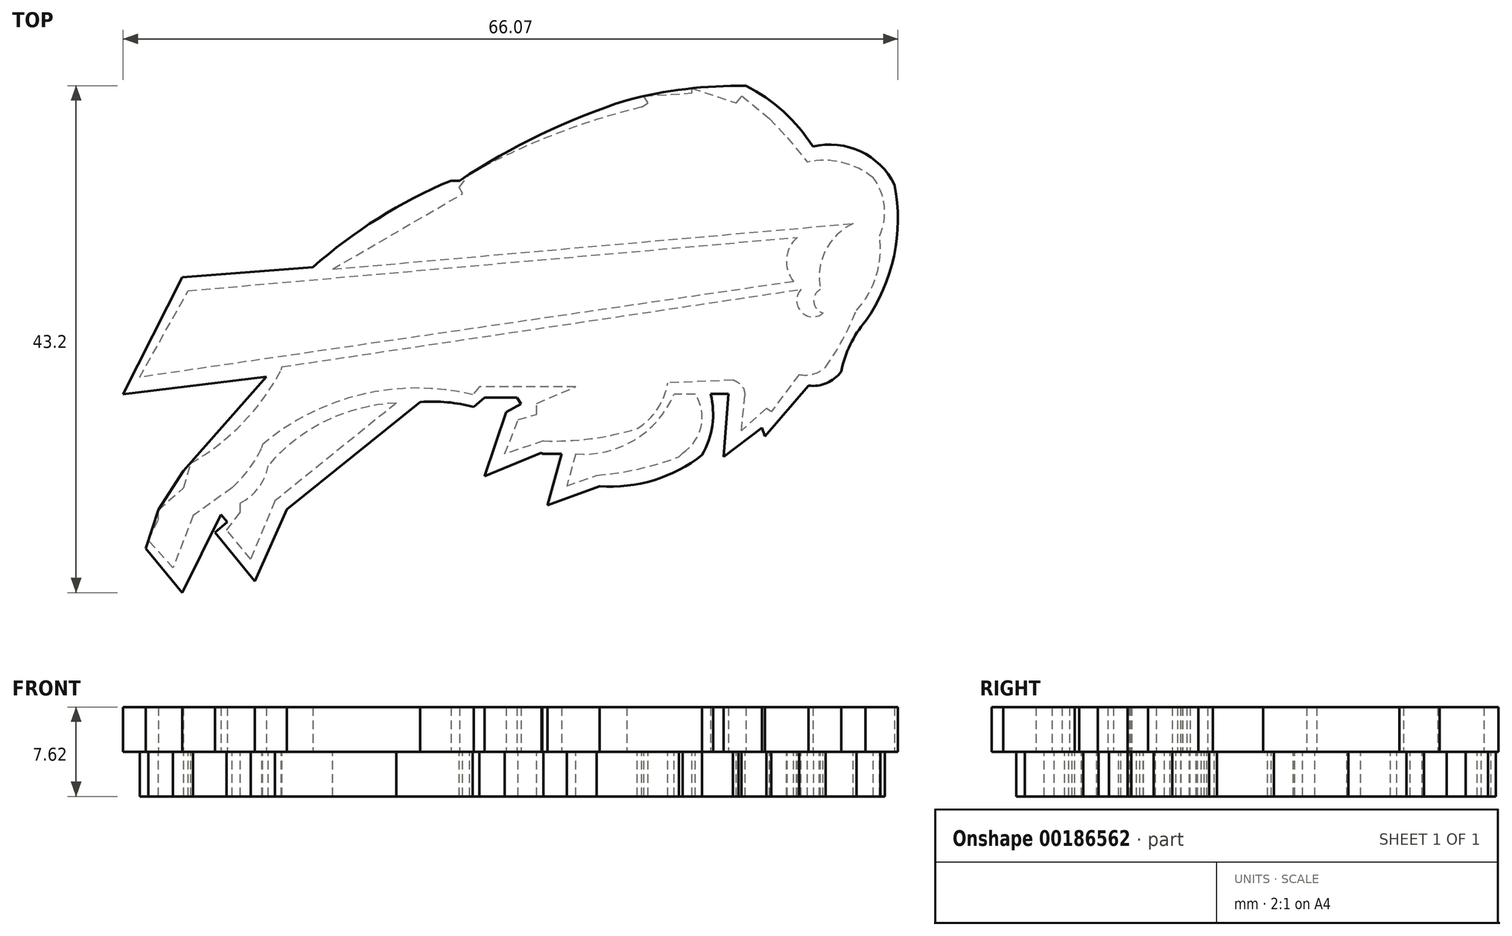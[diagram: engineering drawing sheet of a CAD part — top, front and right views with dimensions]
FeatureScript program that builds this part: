
annotation { "Feature Type Name" : "Feature", "Feature Type Description" : "" }
export const myFeature = defineFeature(function(context is Context, id is Id, definition is map)
    precondition{}
    {
        {
            var Q0;
            Q0=qCreatedBy(makeId("Top.planeOp"),FACE);
            var sketch = newSketch(context, id + "F0", { "sketchPlane" : qUnion([Q0])});
            skLineSegment(sketch, "E0", {"start": v(19.7, -52.96) * mm, "end": v(31.08, -43.8) * mm});
            skArc(sketch, "E1", {"start": v(35.62, -44.21) * mm, "mid": v(33.37, -43.82) * mm, "end": v(31.08, -43.8) * mm});
            skLineSegment(sketch, "E2", {"start": v(35.62, -44.21) * mm, "end": v(36.54, -43.41) * mm});
            skLineSegment(sketch, "E3", {"start": v(36.54, -43.41) * mm, "end": v(39.3, -43.41) * mm});
            skLineSegment(sketch, "E4", {"start": v(39.3, -43.41) * mm, "end": v(39.66, -43.95) * mm});
            skLineSegment(sketch, "E5", {"start": v(39.66, -43.95) * mm, "end": v(38.4, -44.66) * mm});
            skLineSegment(sketch, "E6", {"start": v(38.4, -44.66) * mm, "end": v(36.54, -50.13) * mm});
            skLineSegment(sketch, "E7", {"start": v(36.54, -50.13) * mm, "end": v(41.41, -48.1) * mm});
            skLineSegment(sketch, "E8", {"start": v(41.41, -48.1) * mm, "end": v(41.46, -48.23) * mm});
            skLineSegment(sketch, "E9", {"start": v(41.46, -48.23) * mm, "end": v(43.12, -48.23) * mm});
            skLineSegment(sketch, "E10", {"start": v(43.12, -48.23) * mm, "end": v(41.9, -52.58) * mm});
            skLineSegment(sketch, "E11", {"start": v(41.9, -52.58) * mm, "end": v(46.38, -50.97) * mm});
            skArc(sketch, "E12", {"start": v(46.38, -50.97) * mm, "mid": v(51, -50.46) * mm, "end": v(55.1, -48.3) * mm});
            skArc(sketch, "E13", {"start": v(55.1, -48.3) * mm, "mid": v(55.97, -45.78) * mm, "end": v(55.83, -43.1) * mm});
            skLineSegment(sketch, "E14", {"start": v(55.83, -43.1) * mm, "end": v(57.36, -43.1) * mm});
            skLineSegment(sketch, "E15", {"start": v(56.93, -48.45) * mm, "end": v(57.36, -43.1) * mm});
            skLineSegment(sketch, "E16", {"start": v(56.93, -48.45) * mm, "end": v(60.22, -46) * mm});
            skLineSegment(sketch, "E17", {"start": v(60.22, -46) * mm, "end": v(60.46, -46.7) * mm});
            skLineSegment(sketch, "E18", {"start": v(60.46, -46.7) * mm, "end": v(64.17, -42.4) * mm});
            skArc(sketch, "E19", {"start": v(64.17, -42.4) * mm, "mid": v(65.73, -42.18) * mm, "end": v(66.96, -41.19) * mm});
            skArc(sketch, "E20", {"start": v(69.03, -36.9) * mm, "mid": v(67.73, -38.92) * mm, "end": v(66.96, -41.19) * mm});
            skArc(sketch, "E21", {"start": v(69.03, -36.9) * mm, "mid": v(71.47, -31.35) * mm, "end": v(71.51, -25.29) * mm});
            skArc(sketch, "E22", {"start": v(71.51, -25.29) * mm, "mid": v(68.6, -22.42) * mm, "end": v(64.55, -22.02) * mm});
            skArc(sketch, "E23", {"start": v(64.55, -22.02) * mm, "mid": v(62.04, -19.04) * mm, "end": v(58.83, -16.84) * mm});
            skLineSegment(sketch, "E24", {"start": v(19.7, -52.96) * mm, "end": v(16.98, -59.06) * mm});
            skLineSegment(sketch, "E25", {"start": v(16.98, -59.06) * mm, "end": v(13.55, -54.9) * mm});
            skLineSegment(sketch, "E26", {"start": v(13.55, -54.9) * mm, "end": v(14.6, -54.03) * mm});
            skLineSegment(sketch, "E27", {"start": v(14.6, -54.03) * mm, "end": v(14.08, -53.4) * mm});
            skPoint(sketch, "E27.endSnap0", {"position": v(14.08, -54.46) * mm});
            skLineSegment(sketch, "E28", {"start": v(14.08, -53.4) * mm, "end": v(10.77, -60.04) * mm});
            skLineSegment(sketch, "E29", {"start": v(10.77, -60.04) * mm, "end": v(7.65, -56.27) * mm});
            skLineSegment(sketch, "E30", {"start": v(7.65, -56.27) * mm, "end": v(8.73, -52.98) * mm});
            skLineSegment(sketch, "E31", {"start": v(8.73, -52.98) * mm, "end": v(10.87, -49.66) * mm});
            skLineSegment(sketch, "E32", {"start": v(10.87, -49.66) * mm, "end": v(17.94, -41.63) * mm});
            skLineSegment(sketch, "E33", {"start": v(17.94, -41.63) * mm, "end": v(5.73, -43.13) * mm});
            skLineSegment(sketch, "E34", {"start": v(5.73, -43.13) * mm, "end": v(10.77, -33.17) * mm});
            skLineSegment(sketch, "E35", {"start": v(10.77, -33.17) * mm, "end": v(21.9, -32.31) * mm});
            skArc(sketch, "E36", {"start": v(33.68, -24.92) * mm, "mid": v(27.49, -28.14) * mm, "end": v(21.9, -32.31) * mm});
            skArc(sketch, "E37", {"start": v(48.67, -18.07) * mm, "mid": v(41.31, -21) * mm, "end": v(34.43, -24.92) * mm});
            skArc(sketch, "E38", {"start": v(58.83, -16.84) * mm, "mid": v(53.7, -17.12) * mm, "end": v(48.67, -18.07) * mm});
            skLineSegment(sketch, "E39", {"start": v(33.68, -24.92) * mm, "end": v(34.43, -24.92) * mm});
            skSolve(sketch);
        }
        {
            var Q0;
            Q0 = qSketchRegion(id + "F0", true);
            extrude(context, id + "F1", {"entities" : qUnion([Q0]), "depth" : 3.8 * mm});
        }
        {
            var Q0;
            Q0=makeQuery(id+"F1.opExtrude","CAP_FACE",FACE,{"disambiguationData":[OSD([sQuery(id+"F0.wireOp",EDGE,"E0"),sQuery(id+"F0.wireOp",EDGE,"E1"),sQuery(id+"F0.wireOp",EDGE,"E2"),sQuery(id+"F0.wireOp",EDGE,"E3"),sQuery(id+"F0.wireOp",EDGE,"E4"),sQuery(id+"F0.wireOp",EDGE,"E5"),sQuery(id+"F0.wireOp",EDGE,"E6"),sQuery(id+"F0.wireOp",EDGE,"E7"),sQuery(id+"F0.wireOp",EDGE,"E8"),sQuery(id+"F0.wireOp",EDGE,"E9"),sQuery(id+"F0.wireOp",EDGE,"E10"),sQuery(id+"F0.wireOp",EDGE,"E11"),sQuery(id+"F0.wireOp",EDGE,"E12"),sQuery(id+"F0.wireOp",EDGE,"E13"),sQuery(id+"F0.wireOp",EDGE,"E14"),sQuery(id+"F0.wireOp",EDGE,"E15"),sQuery(id+"F0.wireOp",EDGE,"E16"),sQuery(id+"F0.wireOp",EDGE,"E17"),sQuery(id+"F0.wireOp",EDGE,"E18"),sQuery(id+"F0.wireOp",EDGE,"E19"),sQuery(id+"F0.wireOp",EDGE,"E20"),sQuery(id+"F0.wireOp",EDGE,"E21"),sQuery(id+"F0.wireOp",EDGE,"E22"),sQuery(id+"F0.wireOp",EDGE,"E23"),sQuery(id+"F0.wireOp",EDGE,"E24"),sQuery(id+"F0.wireOp",EDGE,"E25"),sQuery(id+"F0.wireOp",EDGE,"E26"),sQuery(id+"F0.wireOp",EDGE,"E27"),sQuery(id+"F0.wireOp",EDGE,"E28"),sQuery(id+"F0.wireOp",EDGE,"E29"),sQuery(id+"F0.wireOp",EDGE,"E30"),sQuery(id+"F0.wireOp",EDGE,"E31"),sQuery(id+"F0.wireOp",EDGE,"E32"),sQuery(id+"F0.wireOp",EDGE,"E33"),sQuery(id+"F0.wireOp",EDGE,"E34"),sQuery(id+"F0.wireOp",EDGE,"E35"),sQuery(id+"F0.wireOp",EDGE,"E36"),sQuery(id+"F0.wireOp",EDGE,"E37"),sQuery(id+"F0.wireOp",EDGE,"E38"),sQuery(id+"F0.wireOp",EDGE,"E39")])],"isStart":true});
            var sketch = newSketch(context, id + "F2", { "sketchPlane" : qUnion([Q0])});
            skArc(sketch, "E40", {"start": v(64.07, 23.34) * mm, "mid": v(67.04, 23.38) * mm, "end": v(69.7, 24.68) * mm});
            skArc(sketch, "E41", {"start": v(69.7, 24.68) * mm, "mid": v(70.64, 27.08) * mm, "end": v(70.23, 29.63) * mm});
            skArc(sketch, "E42", {"start": v(70.23, 29.63) * mm, "mid": v(69.96, 33.03) * mm, "end": v(68.26, 35.98) * mm});
            skArc(sketch, "E43", {"start": v(68.26, 35.98) * mm, "mid": v(67.08, 38.48) * mm, "end": v(65.64, 40.83) * mm});
            skArc(sketch, "E44", {"start": v(65.64, 40.83) * mm, "mid": v(64.57, 41.4) * mm, "end": v(63.37, 41.45) * mm});
            skLineSegment(sketch, "E45", {"start": v(63.37, 41.45) * mm, "end": v(61, 44.63) * mm});
            skLineSegment(sketch, "E46", {"start": v(61, 44.63) * mm, "end": v(60.6, 44.33) * mm});
            skLineSegment(sketch, "E47", {"start": v(60.6, 44.33) * mm, "end": v(58.45, 46.23) * mm});
            skLineSegment(sketch, "E48", {"start": v(58.45, 46.23) * mm, "end": v(58.76, 43.26) * mm});
            skArc(sketch, "E49", {"start": v(58.2, 42.17) * mm, "mid": v(58.64, 42.63) * mm, "end": v(58.76, 43.26) * mm});
            skArc(sketch, "E50", {"start": v(57.72, 41.93) * mm, "mid": v(57.97, 42.03) * mm, "end": v(58.2, 42.17) * mm});
            skLineSegment(sketch, "E51", {"start": v(57.72, 41.93) * mm, "end": v(52.19, 42.17) * mm});
            skArc(sketch, "E52", {"start": v(52.19, 42.17) * mm, "mid": v(51.3, 44.4) * mm, "end": v(49.58, 46.06) * mm});
            skArc(sketch, "E53", {"start": v(49.58, 46.06) * mm, "mid": v(45.62, 46.92) * mm, "end": v(41.58, 47.1) * mm});
            skLineSegment(sketch, "E54", {"start": v(41.58, 47.1) * mm, "end": v(38.28, 48.23) * mm});
            skLineSegment(sketch, "E55", {"start": v(38.28, 48.23) * mm, "end": v(39.41, 45.3) * mm});
            skLineSegment(sketch, "E56", {"start": v(39.41, 45.3) * mm, "end": v(41.01, 44.85) * mm});
            skLineSegment(sketch, "E57", {"start": v(41.01, 44.85) * mm, "end": v(41.01, 43.91) * mm});
            skLineSegment(sketch, "E58", {"start": v(41.01, 43.91) * mm, "end": v(44.32, 42.49) * mm});
            skLineSegment(sketch, "E59", {"start": v(44.32, 42.49) * mm, "end": v(36.12, 42.49) * mm});
            skLineSegment(sketch, "E60", {"start": v(36.12, 42.49) * mm, "end": v(35.54, 43.17) * mm});
            skArc(sketch, "E61", {"start": v(17.62, 47.41) * mm, "mid": v(26.07, 43.15) * mm, "end": v(35.54, 43.17) * mm});
            skArc(sketch, "E62", {"start": v(17.57, 47.7) * mm, "mid": v(16.46, 49.52) * mm, "end": v(15.02, 51.1) * mm});
            skLineSegment(sketch, "E63", {"start": v(17.57, 47.7) * mm, "end": v(17.62, 47.41) * mm});
            skLineSegment(sketch, "E64", {"start": v(15.02, 51.1) * mm, "end": v(11.7, 53.48) * mm});
            skLineSegment(sketch, "E65", {"start": v(11.7, 53.48) * mm, "end": v(9.99, 57.94) * mm});
            skLineSegment(sketch, "E66", {"start": v(9.99, 57.94) * mm, "end": v(7.88, 55.57) * mm});
            skLineSegment(sketch, "E67", {"start": v(7.88, 55.57) * mm, "end": v(8.73, 53.84) * mm});
            skLineSegment(sketch, "E68", {"start": v(8.73, 53.84) * mm, "end": v(8.73, 52.98) * mm});
            skLineSegment(sketch, "E69", {"start": v(8.73, 52.98) * mm, "end": v(10.91, 51.1) * mm});
            skLineSegment(sketch, "E70", {"start": v(10.91, 51.1) * mm, "end": v(11.55, 48.89) * mm});
            skArc(sketch, "E71", {"start": v(19.22, 41.07) * mm, "mid": v(15.87, 45.65) * mm, "end": v(11.36, 49.1) * mm});
            skLineSegment(sketch, "E72", {"start": v(23.6, 32.47) * mm, "end": v(34.69, 26.03) * mm});
            skLineSegment(sketch, "E73", {"start": v(34.69, 26.03) * mm, "end": v(34.38, 25.5) * mm});
            skLineSegment(sketch, "E74", {"start": v(34.38, 25.5) * mm, "end": v(35.28, 24.37) * mm});
            skArc(sketch, "E75", {"start": v(35.28, 24.37) * mm, "mid": v(42.42, 21.02) * mm, "end": v(49.94, 18.65) * mm});
            skLineSegment(sketch, "E76", {"start": v(49.94, 18.65) * mm, "end": v(50.5, 18.3) * mm});
            skLineSegment(sketch, "E77", {"start": v(50.5, 18.3) * mm, "end": v(50.14, 17.72) * mm});
            skLineSegment(sketch, "E78", {"start": v(50.14, 17.72) * mm, "end": v(54.22, 17.46) * mm});
            skLineSegment(sketch, "E79", {"start": v(54.22, 17.46) * mm, "end": v(54.22, 17.06) * mm});
            skLineSegment(sketch, "E80", {"start": v(54.22, 17.06) * mm, "end": v(58.02, 18.3) * mm});
            skLineSegment(sketch, "E81", {"start": v(58.02, 18.3) * mm, "end": v(58.5, 17.71) * mm});
            skLineSegment(sketch, "E82", {"start": v(58.5, 17.71) * mm, "end": v(60.84, 19.63) * mm});
            skLineSegment(sketch, "E83", {"start": v(60.84, 19.63) * mm, "end": v(62.36, 21.26) * mm});
            skLineSegment(sketch, "E84", {"start": v(62.36, 21.26) * mm, "end": v(64.07, 23.34) * mm});
            skLineSegment(sketch, "E85", {"start": v(23.6, 32.47) * mm, "end": v(67.98, 28.58) * mm});
            skArc(sketch, "E86", {"start": v(65.2, 34.2) * mm, "mid": v(65.61, 30.9) * mm, "end": v(67.98, 28.58) * mm});
            skArc(sketch, "E87", {"start": v(65.43, 36.21) * mm, "mid": v(64.62, 35.28) * mm, "end": v(65.2, 34.2) * mm});
            skArc(sketch, "E88", {"start": v(65.43, 36.21) * mm, "mid": v(63.53, 36.1) * mm, "end": v(63.54, 34.2) * mm});
            skArc(sketch, "E89", {"start": v(54.52, 43.13) * mm, "mid": v(55.02, 45.86) * mm, "end": v(53.44, 48.14) * mm});
            skArc(sketch, "E90", {"start": v(53.13, 48.46) * mm, "mid": v(49.68, 49.5) * mm, "end": v(46.11, 50.04) * mm});
            skLineSegment(sketch, "E91", {"start": v(54.52, 43.13) * mm, "end": v(52.72, 43.13) * mm});
            skArc(sketch, "E92", {"start": v(52.72, 43.13) * mm, "mid": v(49.34, 47.03) * mm, "end": v(44.32, 48.23) * mm});
            skLineSegment(sketch, "E93", {"start": v(44.32, 48.23) * mm, "end": v(43.58, 50.93) * mm});
            skLineSegment(sketch, "E94", {"start": v(43.58, 50.93) * mm, "end": v(46.11, 50.04) * mm});
            skLineSegment(sketch, "E95", {"start": v(16.6, 57.2) * mm, "end": v(14.55, 54.7) * mm});
            skLineSegment(sketch, "E96", {"start": v(14.55, 54.7) * mm, "end": v(15.73, 53.2) * mm});
            skLineSegment(sketch, "E97", {"start": v(15.73, 53.2) * mm, "end": v(15.73, 52.4) * mm});
            skArc(sketch, "E98", {"start": v(18.1, 49.22) * mm, "mid": v(17.3, 51.1) * mm, "end": v(15.73, 52.4) * mm});
            skArc(sketch, "E99", {"start": v(18.1, 49.22) * mm, "mid": v(23, 45.41) * mm, "end": v(29.02, 43.89) * mm});
            skLineSegment(sketch, "E100", {"start": v(29.02, 43.89) * mm, "end": v(18.67, 52.22) * mm});
            skLineSegment(sketch, "E101", {"start": v(18.67, 52.22) * mm, "end": v(16.6, 57.2) * mm});
            skPoint(sketch, "E102.end.orphan", {"position": v(5.88, 42.84) * mm});
            skLineSegment(sketch, "E103", {"start": v(19.22, 41.07) * mm, "end": v(19.29, 40.8) * mm});
            skLineSegment(sketch, "E104", {"start": v(19.29, 40.8) * mm, "end": v(63.54, 34.2) * mm});
            skLineSegment(sketch, "E105", {"start": v(53.44, 48.14) * mm, "end": v(53.13, 48.46) * mm});
            skSolve(sketch);
        }
        {
            var Q0;
            Q0 = qSketchRegion(id + "F2", true);
            extrude(context, id + "F3", {"entities" : qUnion([Q0]), "operationType" : NewBodyOperationType.ADD, "depth" : 3.8 * mm});
        }
        {
            var Q0;
            {var subQ0=sQuery(id+"F0.wireOp",EDGE,"E39");var subQ1=sQuery(id+"F0.wireOp",EDGE,"E30");var subQ2=sQuery(id+"F0.wireOp",EDGE,"E32");var subQ3=sQuery(id+"F0.wireOp",EDGE,"E31");var subQ4=sQuery(id+"F0.wireOp",EDGE,"E37");var subQ5=sQuery(id+"F0.wireOp",EDGE,"E36");var subQ6=sQuery(id+"F0.wireOp",EDGE,"E35");var subQ7=sQuery(id+"F0.wireOp",EDGE,"E34");var subQ8=sQuery(id+"F0.wireOp",EDGE,"E33");var subQ9=makeQuery(id+"F1.opExtrude","CAP_FACE",FACE,{"disambiguationData":[OSD([sQuery(id+"F0.wireOp",EDGE,"E0"),sQuery(id+"F0.wireOp",EDGE,"E1"),sQuery(id+"F0.wireOp",EDGE,"E2"),sQuery(id+"F0.wireOp",EDGE,"E3"),sQuery(id+"F0.wireOp",EDGE,"E4"),sQuery(id+"F0.wireOp",EDGE,"E5"),sQuery(id+"F0.wireOp",EDGE,"E6"),sQuery(id+"F0.wireOp",EDGE,"E7"),sQuery(id+"F0.wireOp",EDGE,"E8"),sQuery(id+"F0.wireOp",EDGE,"E9"),sQuery(id+"F0.wireOp",EDGE,"E10"),sQuery(id+"F0.wireOp",EDGE,"E11"),sQuery(id+"F0.wireOp",EDGE,"E12"),sQuery(id+"F0.wireOp",EDGE,"E13"),sQuery(id+"F0.wireOp",EDGE,"E14"),sQuery(id+"F0.wireOp",EDGE,"E15"),sQuery(id+"F0.wireOp",EDGE,"E16"),sQuery(id+"F0.wireOp",EDGE,"E17"),sQuery(id+"F0.wireOp",EDGE,"E18"),sQuery(id+"F0.wireOp",EDGE,"E19"),sQuery(id+"F0.wireOp",EDGE,"E20"),sQuery(id+"F0.wireOp",EDGE,"E21"),sQuery(id+"F0.wireOp",EDGE,"E22"),sQuery(id+"F0.wireOp",EDGE,"E23"),sQuery(id+"F0.wireOp",EDGE,"E24"),sQuery(id+"F0.wireOp",EDGE,"E25"),sQuery(id+"F0.wireOp",EDGE,"E26"),sQuery(id+"F0.wireOp",EDGE,"E27"),sQuery(id+"F0.wireOp",EDGE,"E28"),sQuery(id+"F0.wireOp",EDGE,"E29"),subQ1,subQ3,subQ2,subQ8,subQ7,subQ6,subQ5,subQ4,sQuery(id+"F0.wireOp",EDGE,"E38"),subQ0])],"isStart":true});Q0=makeQuery(id+"F3.boolean.opBoolean","SPLIT",FACE,{"disambiguationData":[TD([subQ9,makeQuery(id+"F1.opExtrude","SWEPT_FACE",FACE,{"disambiguationData":[OSD([subQ1])]}),makeQuery(id+"F1.opExtrude","SWEPT_FACE",FACE,{"disambiguationData":[OSD([subQ3])]}),makeQuery(id+"F1.opExtrude","SWEPT_FACE",FACE,{"disambiguationData":[OSD([subQ2])]}),makeQuery(id+"F1.opExtrude","SWEPT_FACE",FACE,{"disambiguationData":[OSD([subQ8])]}),makeQuery(id+"F1.opExtrude","SWEPT_FACE",FACE,{"disambiguationData":[OSD([subQ7])]}),makeQuery(id+"F1.opExtrude","SWEPT_FACE",FACE,{"disambiguationData":[OSD([subQ6])]}),makeQuery(id+"F1.opExtrude","SWEPT_FACE",FACE,{"disambiguationData":[OSD([subQ5])]}),makeQuery(id+"F1.opExtrude","SWEPT_FACE",FACE,{"disambiguationData":[OSD([subQ4])]}),makeQuery(id+"F1.opExtrude","SWEPT_FACE",FACE,{"disambiguationData":[OSD([subQ0])]}),makeQuery(id+"F3.opExtrude","SWEPT_FACE",FACE,{"disambiguationData":[OSD([sQuery(id+"F2.wireOp",EDGE,"E68")])]}),makeQuery(id+"F3.opExtrude","SWEPT_FACE",FACE,{"disambiguationData":[OSD([sQuery(id+"F2.wireOp",EDGE,"E69")])]}),makeQuery(id+"F3.opExtrude","SWEPT_FACE",FACE,{"disambiguationData":[OSD([sQuery(id+"F2.wireOp",EDGE,"E70")])]}),makeQuery(id+"F3.opExtrude","SWEPT_FACE",FACE,{"disambiguationData":[OSD([sQuery(id+"F2.wireOp",EDGE,"E71")])]}),makeQuery(id+"F3.opExtrude","SWEPT_FACE",FACE,{"disambiguationData":[OSD([sQuery(id+"F2.wireOp",EDGE,"E72")])]}),makeQuery(id+"F3.opExtrude","SWEPT_FACE",FACE,{"disambiguationData":[OSD([sQuery(id+"F2.wireOp",EDGE,"E73")])]}),makeQuery(id+"F3.opExtrude","SWEPT_FACE",FACE,{"disambiguationData":[OSD([sQuery(id+"F2.wireOp",EDGE,"E74")])]}),makeQuery(id+"F3.opExtrude","SWEPT_FACE",FACE,{"disambiguationData":[OSD([sQuery(id+"F2.wireOp",EDGE,"E75")])]}),makeQuery(id+"F3.opExtrude","SWEPT_FACE",FACE,{"disambiguationData":[OSD([sQuery(id+"F2.wireOp",EDGE,"E85")])]}),makeQuery(id+"F3.opExtrude","SWEPT_FACE",FACE,{"disambiguationData":[OSD([sQuery(id+"F2.wireOp",EDGE,"E86")])]}),makeQuery(id+"F3.opExtrude","SWEPT_FACE",FACE,{"disambiguationData":[OSD([sQuery(id+"F2.wireOp",EDGE,"E87")])]}),makeQuery(id+"F3.opExtrude","SWEPT_FACE",FACE,{"disambiguationData":[OSD([sQuery(id+"F2.wireOp",EDGE,"E88")])]}),makeQuery(id+"F3.opExtrude","SWEPT_FACE",FACE,{"disambiguationData":[OSD([sQuery(id+"F2.wireOp",EDGE,"E103")])]}),makeQuery(id+"F3.opExtrude","SWEPT_FACE",FACE,{"disambiguationData":[OSD([sQuery(id+"F2.wireOp",EDGE,"E104")])]})])],"derivedFrom":subQ9});}
            var sketch = newSketch(context, id + "F4", { "sketchPlane" : qUnion([Q0])});
            skLineSegment(sketch, "E106", {"start": v(62.9, 33.53) * mm, "end": v(7.14, 41.69) * mm});
            skLineSegment(sketch, "E107", {"start": v(7.14, 41.69) * mm, "end": v(11.28, 34.31) * mm});
            skLineSegment(sketch, "E108", {"start": v(11.28, 34.31) * mm, "end": v(63.38, 29.74) * mm});
            skArc(sketch, "E109", {"start": v(62.9, 33.53) * mm, "mid": v(62.3, 31.58) * mm, "end": v(63.22, 29.76) * mm});
            skSolve(sketch);
        }
        {
            var Q0;
            Q0 = qSketchRegion(id + "F4", true);
            extrude(context, id + "F5", {"entities" : qUnion([Q0]), "operationType" : NewBodyOperationType.ADD, "depth" : 3.8 * mm});
        }
    });
